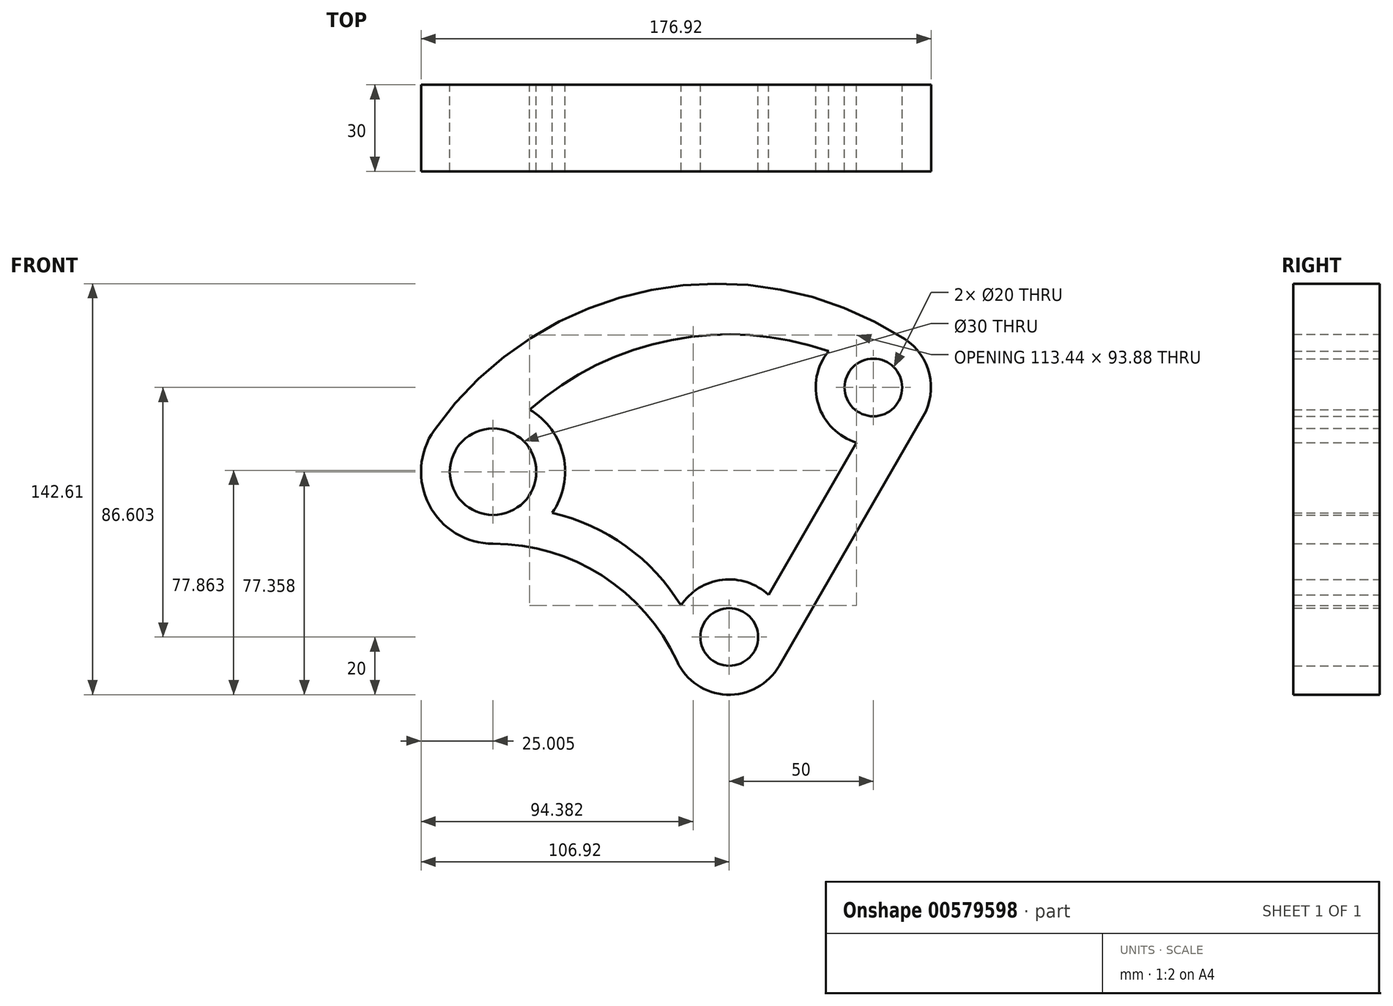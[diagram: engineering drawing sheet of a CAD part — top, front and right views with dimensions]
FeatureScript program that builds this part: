
annotation { "Feature Type Name" : "Feature", "Feature Type Description" : "" }
export const myFeature = defineFeature(function(context is Context, id is Id, definition is map)
    precondition{}
    {
        {
            var Q0;
            Q0=qCreatedBy(makeId("Front.planeOp"),FACE);
            var sketch = newSketch(context, id + "F0", { "sketchPlane" : qUnion([Q0])});
            skCircle(sketch, "E0", {"center": v(0, 0) * mm, "radius": 10 * mm});
            skCircle(sketch, "E1", {"center": v(-81.92, 57.36) * mm, "radius": 15 * mm});
            skCircle(sketch, "E2", {"center": v(50, 86.6) * mm, "radius": 10 * mm});
            skArc(sketch, "E3", {"start": v(-18.15, -8.4) * mm, "mid": v(-0.9, -19.98) * mm, "end": v(17.32, -10) * mm});
            skArc(sketch, "E4", {"start": v(-102.35, 71.76) * mm, "mid": v(-104.1, 45.85) * mm, "end": v(-81.92, 32.36) * mm});
            skArc(sketch, "E5", {"start": v(34.45, 99.19) * mm, "mid": v(30.88, 80.74) * mm, "end": v(44.18, 67.47) * mm});
            skLineSegment(sketch, "E6", {"start": v(-81.92, 57.36) * mm, "end": v(0, 0) * mm, "construction": true});
            skLineSegment(sketch, "E7", {"start": v(50, 86.6) * mm, "end": v(0, 0) * mm, "construction": true});
            skLineSegment(sketch, "E8", {"start": v(0, 0) * mm, "end": v(0, 134.72) * mm, "construction": true});
            skArc(sketch, "E9", {"start": v(55.43, 95) * mm, "mid": v(-25.2, 110.6) * mm, "end": v(-94.17, 66) * mm, "construction": true});
            skArc(sketch, "E10", {"start": v(34.45, 99.19) * mm, "mid": v(-20.14, 103.05) * mm, "end": v(-69.26, 78.92) * mm});
            skArc(sketch, "E11", {"start": v(60.85, 103.4) * mm, "mid": v(-27.11, 120.42) * mm, "end": v(-102.35, 71.76) * mm});
            skLineSegment(sketch, "E12", {"start": v(67.32, 76.6) * mm, "end": v(17.32, -10) * mm});
            skLineSegment(sketch, "E13", {"start": v(13.66, 14.6) * mm, "end": v(44.18, 67.47) * mm});
            skArc(sketch, "E14", {"start": v(-18.15, -8.4) * mm, "mid": v(-44.08, 21.3) * mm, "end": v(-81.92, 32.36) * mm});
            skArc(sketch, "E15", {"start": v(-16.75, 10.92) * mm, "mid": v(-35.82, 31.53) * mm, "end": v(-61.44, 43.02) * mm});
            skArc(sketch, "E16.trimOffspring", {"start": v(-61.44, 43.02) * mm, "mid": v(-57.49, 62.68) * mm, "end": v(-69.26, 78.92) * mm});
            skArc(sketch, "E17.trimOffspring", {"start": v(13.66, 14.6) * mm, "mid": v(-2.4, 19.86) * mm, "end": v(-16.75, 10.92) * mm});
            skArc(sketch, "E18.trimOffspring", {"start": v(67.32, 76.6) * mm, "mid": v(69.44, 91.3) * mm, "end": v(60.85, 103.4) * mm});
            skSolve(sketch);
        }
        {
            var Q0;
            Q0=qSketchRegion(id+"F0",true);
            extrude(context, id + "F1", {"entities" : qUnion([Q0]), "depth" : 30 * mm, "offsetDistance" : 25 * mm});
        }
    });
